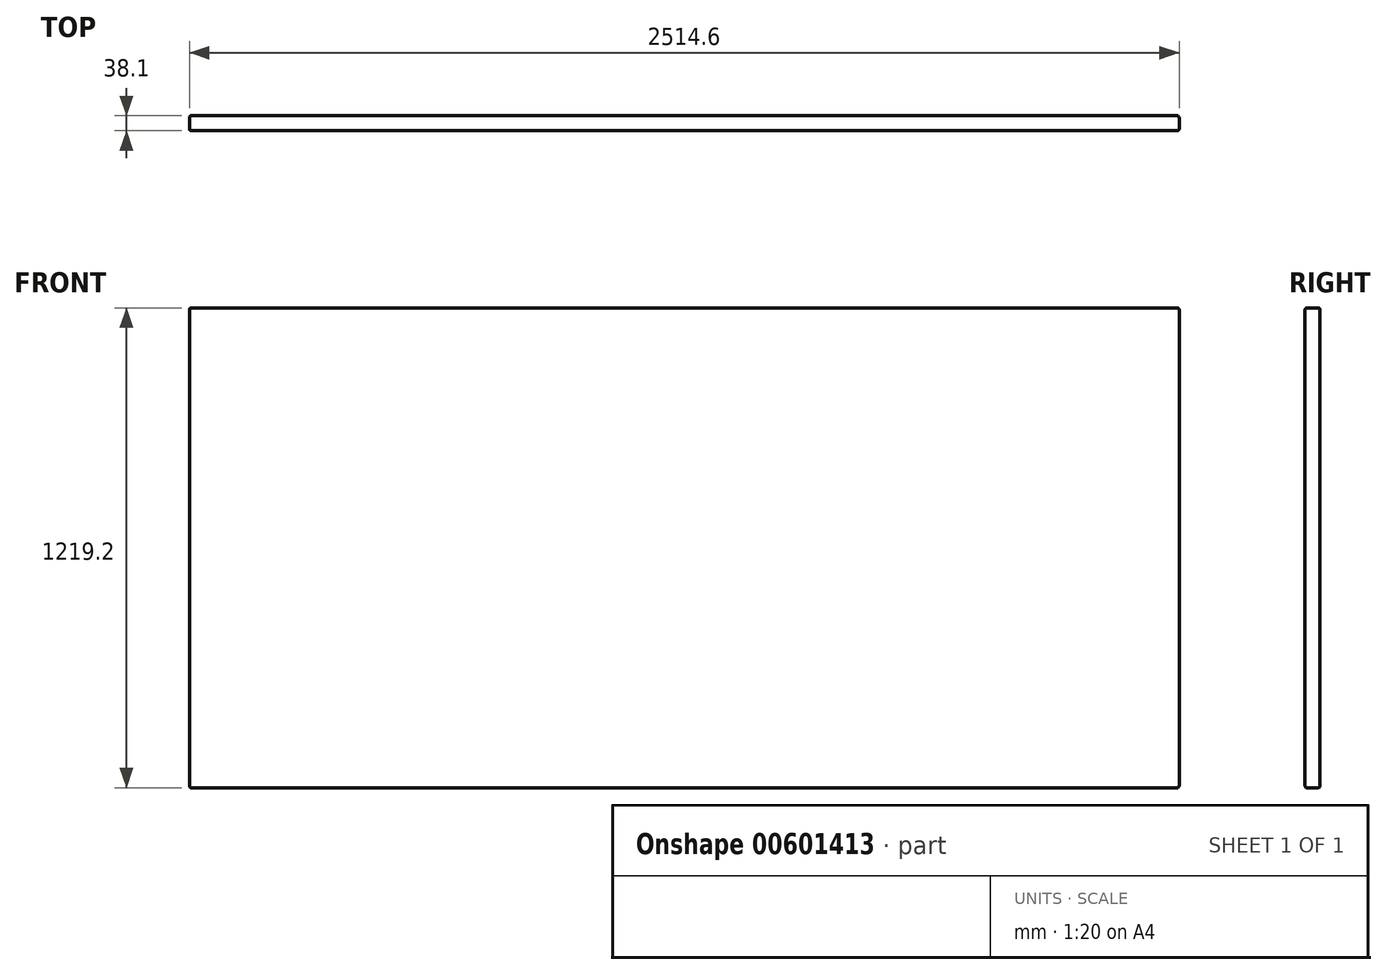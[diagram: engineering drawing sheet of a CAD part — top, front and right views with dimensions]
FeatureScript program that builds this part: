
annotation { "Feature Type Name" : "Feature", "Feature Type Description" : "" }
export const myFeature = defineFeature(function(context is Context, id is Id, definition is map)
    precondition{}
    {
        {
            var Q0;
            Q0=qCreatedBy(makeId("Front.planeOp"),FACE);
            var sketch = newSketch(context, id + "F0", { "sketchPlane" : qUnion([Q0])});
            skLineSegment(sketch, "E0.bottom", {"start": v(0, 0) * mm, "end": v(-2514.6, 0) * mm});
            skLineSegment(sketch, "E0.top", {"start": v(0, 1219.2) * mm, "end": v(-2514.6, 1219.2) * mm});
            skLineSegment(sketch, "E0.left", {"start": v(0, 0) * mm, "end": v(0, 1219.2) * mm});
            skLineSegment(sketch, "E0.right", {"start": v(-2514.6, 0) * mm, "end": v(-2514.6, 1219.2) * mm});
            skSolve(sketch);
        }
        {
            var Q0;
            Q0 = qSketchRegion(id + "F0", true);
            extrude(context, id + "F1", {"entities" : qUnion([Q0]), "depth" : 38.1 * mm, "offsetDistance" : 25.4 * mm});
        }
        {
            var Q0;
            Q0=makeQuery(id+"F1.opExtrude","CAP_EDGE",EDGE,{"disambiguationData":[OSD([sQuery(id+"F0.wireOp",EDGE,"E0.top")])],"isStart":false});
            var Q1;
            Q1=makeQuery(id+"F1.opExtrude","CAP_EDGE",EDGE,{"disambiguationData":[OSD([sQuery(id+"F0.wireOp",EDGE,"E0.left")])],"isStart":false});
            var Q2;
            Q2=makeQuery(id+"F1.opExtrude","CAP_EDGE",EDGE,{"disambiguationData":[OSD([sQuery(id+"F0.wireOp",EDGE,"E0.bottom")])],"isStart":false});
            var Q3;
            Q3=makeQuery(id+"F1.opExtrude","CAP_EDGE",EDGE,{"disambiguationData":[OSD([sQuery(id+"F0.wireOp",EDGE,"E0.right")])],"isStart":false});
            var Q4;
            Q4=makeQuery(id+"F1.opExtrude","SWEPT_FACE",FACE,{"disambiguationData":[OSD([sQuery(id+"F0.wireOp",EDGE,"E0.top")])]});
            var Q5;
            Q5=makeQuery(id+"F1.opExtrude","CAP_EDGE",EDGE,{"disambiguationData":[OSD([sQuery(id+"F0.wireOp",EDGE,"E0.left")])],"isStart":true});
            var Q6;
            Q6=makeQuery(id+"F1.opExtrude","CAP_EDGE",EDGE,{"disambiguationData":[OSD([sQuery(id+"F0.wireOp",EDGE,"E0.bottom")])],"isStart":true});
            var Q7;
            Q7=makeQuery(id+"F1.opExtrude","SWEPT_EDGE",EDGE,{"disambiguationData":[OSD([sQuery(id+"F0.wireOp",EDGE,"E0.bottom"),sQuery(id+"F0.wireOp",EDGE,"E0.left")])]});
            var Q8;
            Q8=makeQuery(id+"F1.opExtrude","SWEPT_EDGE",EDGE,{"disambiguationData":[OSD([sQuery(id+"F0.wireOp",EDGE,"E0.bottom"),sQuery(id+"F0.wireOp",EDGE,"E0.right")])]});
            var Q9;
            Q9=makeQuery(id+"F1.opExtrude","CAP_EDGE",EDGE,{"disambiguationData":[OSD([sQuery(id+"F0.wireOp",EDGE,"E0.right")])],"isStart":true});
            fillet(context, id + "F2", {"entities" : qUnion([Q0, Q1, Q2, Q3, Q4, Q5, Q6, Q7, Q8, Q9]), "radius" : 4.7 * mm, "tangentPropagation" : true, "allowEdgeOverflow" : false});
        }
    });
